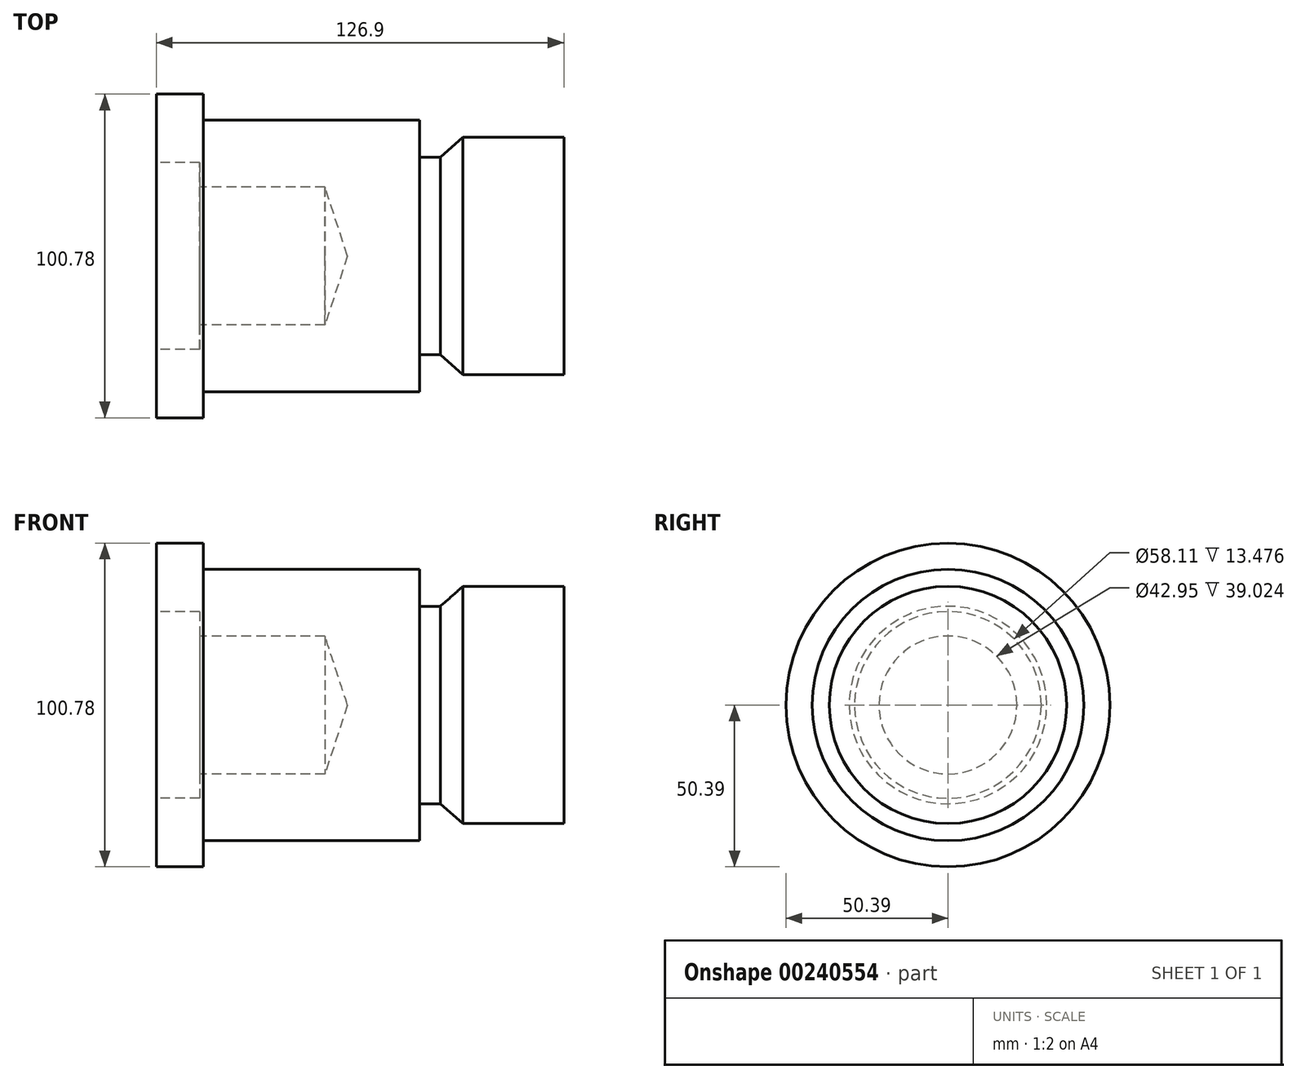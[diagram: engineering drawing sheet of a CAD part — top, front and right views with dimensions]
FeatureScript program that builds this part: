
annotation { "Feature Type Name" : "Feature", "Feature Type Description" : "" }
export const myFeature = defineFeature(function(context is Context, id is Id, definition is map)
    precondition{}
    {
        {
            var Q0;
            Q0=qCreatedBy(makeId("Front.planeOp"),FACE);
            var sketch = newSketch(context, id + "F0", { "sketchPlane" : qUnion([Q0])});
            skLineSegment(sketch, "E0", {"start": v(-67.1, 50.4) * mm, "end": v(-52.5, 50.4) * mm});
            skLineSegment(sketch, "E1", {"start": v(-52.5, 50.4) * mm, "end": v(-52.5, 42.25) * mm});
            skLineSegment(sketch, "E2", {"start": v(-52.5, 42.25) * mm, "end": v(14.88, 42.25) * mm});
            skLineSegment(sketch, "E3", {"start": v(14.88, 42.25) * mm, "end": v(14.88, 30.74) * mm});
            skLineSegment(sketch, "E4", {"start": v(14.88, 30.74) * mm, "end": v(21.34, 30.74) * mm});
            skLineSegment(sketch, "E5", {"start": v(21.34, 30.74) * mm, "end": v(28.36, 36.92) * mm});
            skLineSegment(sketch, "E6", {"start": v(28.36, 36.92) * mm, "end": v(59.8, 36.92) * mm});
            skLineSegment(sketch, "E7", {"start": v(59.8, 36.92) * mm, "end": v(59.8, 0) * mm});
            skLineSegment(sketch, "E8", {"start": v(-67.1, 50.4) * mm, "end": v(-67.1, 29.06) * mm});
            skLineSegment(sketch, "E9", {"start": v(-67.1, 29.06) * mm, "end": v(-53.62, 29.06) * mm});
            skLineSegment(sketch, "E10", {"start": v(-53.62, 29.06) * mm, "end": v(-53.62, 21.48) * mm});
            skLineSegment(sketch, "E11", {"start": v(-53.62, 21.48) * mm, "end": v(-14.6, 21.48) * mm});
            skLineSegment(sketch, "E12", {"start": v(-14.6, 21.48) * mm, "end": v(-7.58, 0) * mm});
            skLineSegment(sketch, "E13", {"start": v(-7.58, 0) * mm, "end": v(59.8, 0) * mm});
            skSolve(sketch);
        }
        {
            var Q0;
            Q0=makeQuery(id+"F0.imprint","IMPRINT",FACE,{"disambiguationData":[TD([[makeQuery(id+"F0.imprint","IMPRINT",EDGE,{"derivedFrom":sQuery(id+"F0.wireOp",EDGE,"E0")}),-1.0]])]});
            var Q1;
            Q1=sQuery(id+"F0.wireOp",EDGE,"E13");
            revolve(context, id + "F1", {"entities" : qUnion([Q0]), "axis" : qUnion([Q1]), "revolveType" : RevolveType.FULL});
        }
    });
